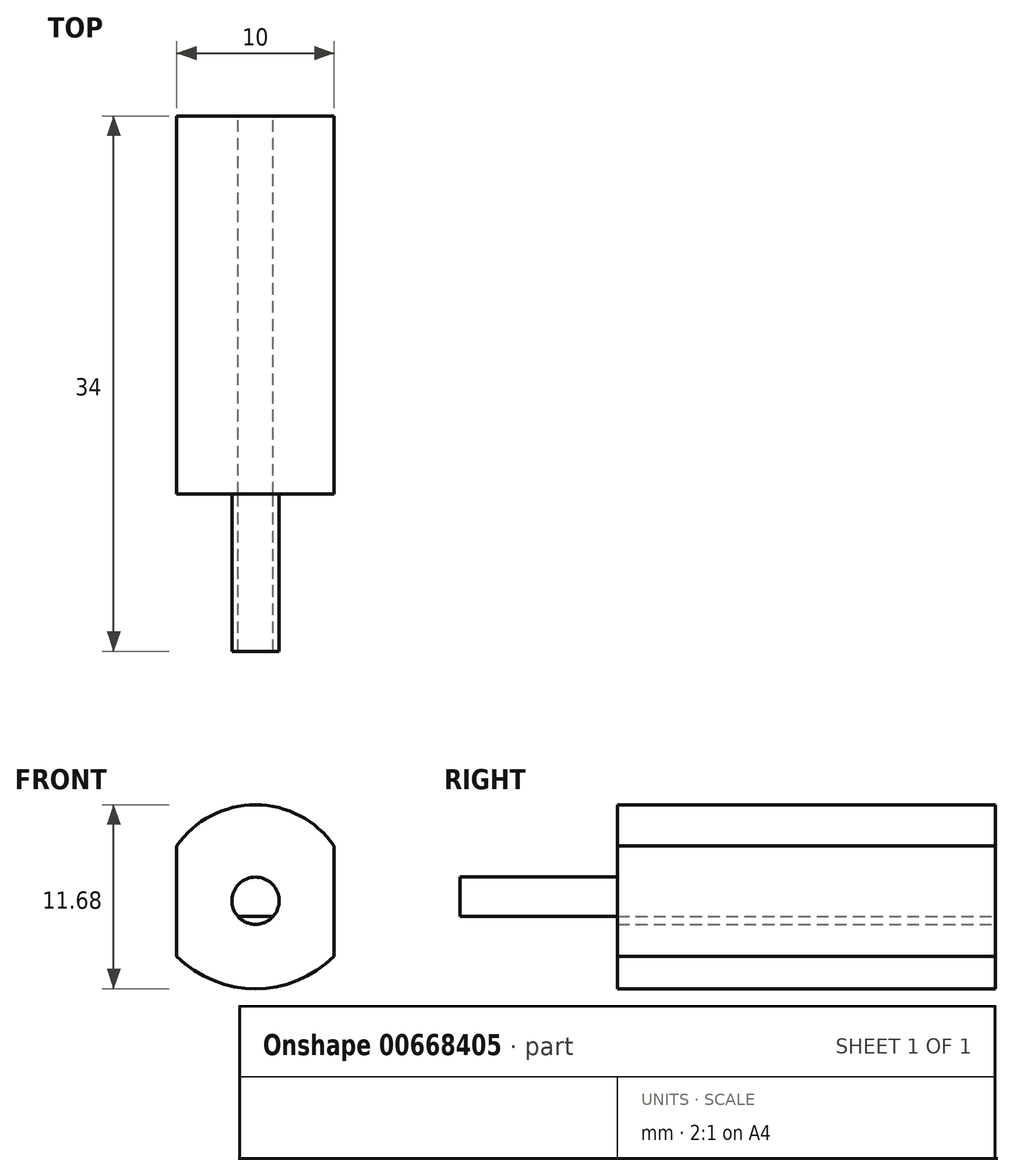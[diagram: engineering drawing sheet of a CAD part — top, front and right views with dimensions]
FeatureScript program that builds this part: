
annotation { "Feature Type Name" : "Feature", "Feature Type Description" : "" }
export const myFeature = defineFeature(function(context is Context, id is Id, definition is map)
    precondition{}
    {
        {
            var Q0;
            Q0=qCreatedBy(makeId("Front.planeOp"),FACE);
            var sketch = newSketch(context, id + "F0", { "sketchPlane" : qUnion([Q0])});
            skLineSegment(sketch, "E0.bottom", {"start": v(-16.62, 2.87) * mm, "end": v(-6.62, 2.87) * mm});
            skLineSegment(sketch, "E0.top", {"start": v(-16.62, -4.13) * mm, "end": v(-6.62, -4.13) * mm});
            skLineSegment(sketch, "E0.left", {"start": v(-16.62, 2.87) * mm, "end": v(-16.62, -4.13) * mm});
            skLineSegment(sketch, "E0.right", {"start": v(-6.62, 2.87) * mm, "end": v(-6.62, -4.13) * mm});
            skArc(sketch, "E1", {"start": v(-6.62, 2.87) * mm, "mid": v(-11.62, 5.49) * mm, "end": v(-16.62, 2.87) * mm});
            skArc(sketch, "E2", {"start": v(-16.62, -4.13) * mm, "mid": v(-11.62, -6.2) * mm, "end": v(-6.62, -4.13) * mm});
            skCircle(sketch, "E3", {"center": v(-11.62, -0.6) * mm, "radius": 1.5 * mm});
            skLineSegment(sketch, "E4", {"start": v(-11.6, -1.6) * mm, "end": v(-12.73, -1.6) * mm});
            skLineSegment(sketch, "E5", {"start": v(-12.73, -1.6) * mm, "end": v(-10.5, -1.6) * mm});
            skSolve(sketch);
        }
        {
            var Q0;
            Q0=makeQuery(id+"F0.imprint","IMPRINT",FACE,{"disambiguationData":[TD([[makeQuery(id+"F0.imprint","IMPRINT",EDGE,{"derivedFrom":sQuery(id+"F0.wireOp",EDGE,"E0.bottom")}),1.0]])]});
            var Q1;
            Q1=makeQuery(id+"F0.imprint","IMPRINT",FACE,{"disambiguationData":[TD([[makeQuery(id+"F0.imprint","IMPRINT",EDGE,{"derivedFrom":sQuery(id+"F0.wireOp",EDGE,"E0.top")}),-1.0]])]});
            var Q2;
            Q2=makeQuery(id+"F0.imprint","IMPRINT",FACE,{"disambiguationData":[TD([[makeQuery(id+"F0.imprint","IMPRINT",EDGE,{"derivedFrom":sQuery(id+"F0.wireOp",EDGE,"E0.bottom")}),-1.0]])]});
            extrude(context, id + "F1", {"entities" : qUnion([Q0, Q1, Q2]), "depth" : 24 * mm, "offsetDistance" : 25 * mm});
        }
        {
            var Q0;
            {var subQ0=sQuery(id+"F0.wireOp",EDGE,"E5");var subQ4=makeQuery(id+"F0.imprint","IMPRINT",VERTEX,{"derivedFrom":subQ0});Q0=makeQuery(id+"F0.imprint","IMPRINT",FACE,{"disambiguationData":[TD([[makeQuery(id+"F0.imprint","IMPRINT",EDGE,{"disambiguationData":[TD([[subQ4,1.0]])],"derivedFrom":subQ0}),1.0]])]});}
            extrude(context, id + "F2", {"entities" : qUnion([Q0]), "operationType" : NewBodyOperationType.ADD, "depth" : 34 * mm, "offsetDistance" : 25 * mm});
        }
    });
